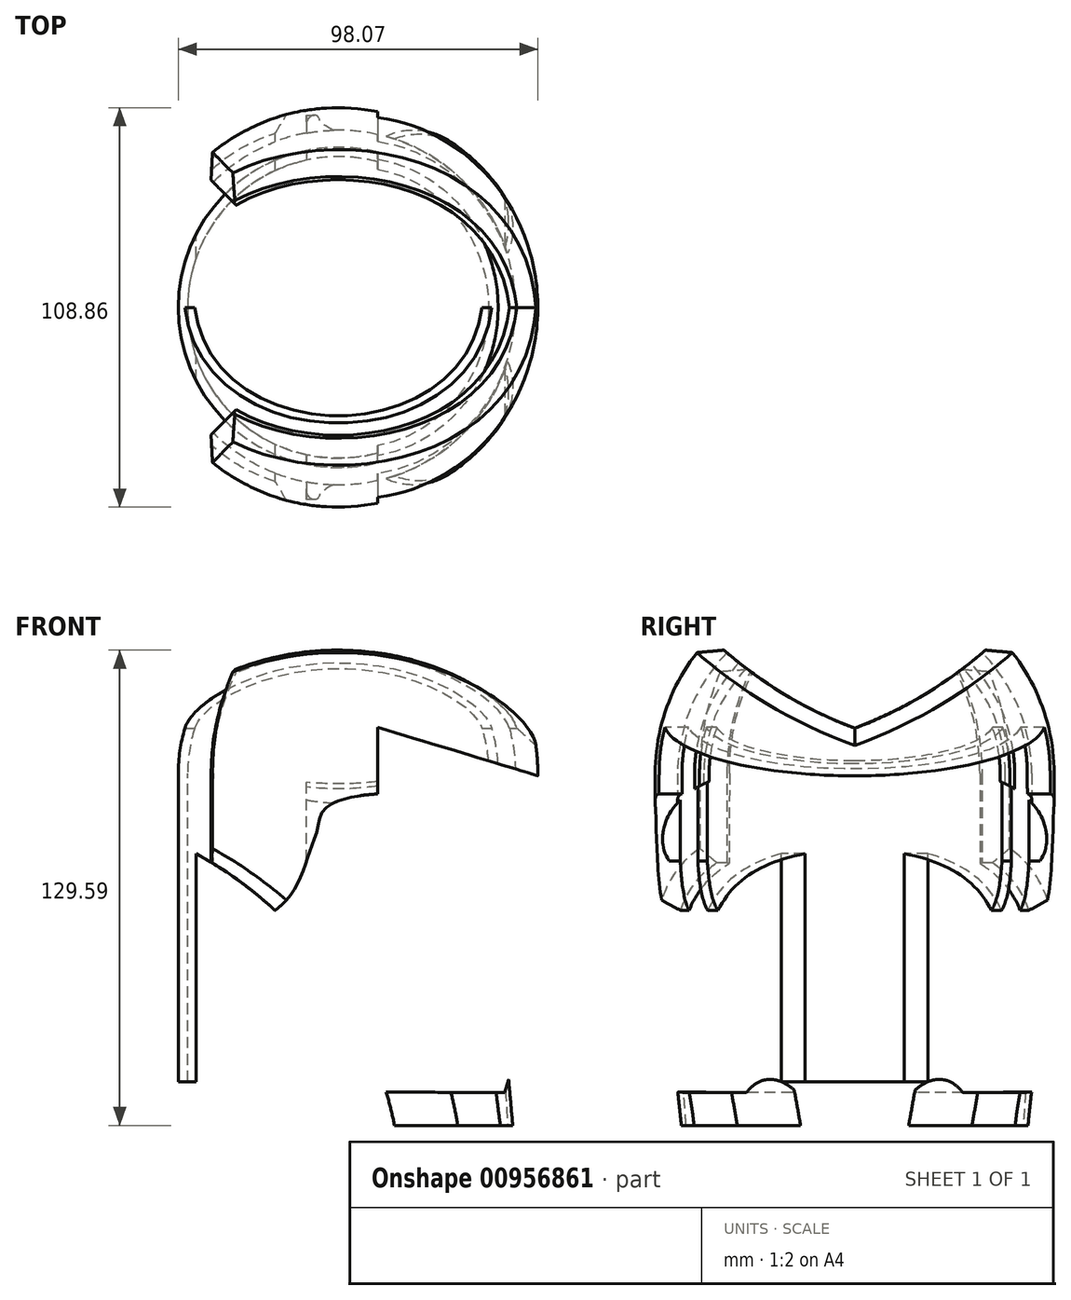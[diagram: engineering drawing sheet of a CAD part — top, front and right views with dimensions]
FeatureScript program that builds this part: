
annotation { "Feature Type Name" : "Feature", "Feature Type Description" : "" }
export const myFeature = defineFeature(function(context is Context, id is Id, definition is map)
    precondition{}
    {
        {
            var Q0;
            Q0=qCreatedBy(makeId("Front.planeOp"),FACE);
            var sketch = newSketch(context, id + "F0", { "sketchPlane" : qUnion([Q0])});
            skLineSegment(sketch, "E0", {"start": v(-40.6, -55.84) * mm, "end": v(-40.6, 28.21) * mm});
            skArc(sketch, "E1", {"start": v(3.06, 71.87) * mm, "mid": v(-27.8, 59.08) * mm, "end": v(-40.6, 28.21) * mm});
            skLineSegment(sketch, "E2", {"start": v(46.72, 28.21) * mm, "end": v(46.72, -55.84) * mm, "construction": true});
            skLineSegment(sketch, "E3", {"start": v(-40.6, -55.84) * mm, "end": v(46.72, -55.84) * mm, "construction": true});
            skLineSegment(sketch, "E4", {"start": v(3.06, 71.87) * mm, "end": v(3.06, -55.84) * mm});
            skArc(sketch, "E5.MirrorCS", {"start": v(3.06, 71.87) * mm, "mid": v(33.93, 59.08) * mm, "end": v(46.72, 28.21) * mm, "construction": true});
            skLineSegment(sketch, "E6", {"start": v(-40.6, -55.84) * mm, "end": v(3.06, -55.84) * mm});
            skLineSegment(sketch, "E7", {"start": v(7.59, 81.6) * mm, "end": v(7.59, 75.09) * mm});
            skArc(sketch, "E8", {"start": v(51.37, 28.17) * mm, "mid": v(38.7, 60.24) * mm, "end": v(7.59, 75.09) * mm});
            skLineSegment(sketch, "E9", {"start": v(51.37, 28.17) * mm, "end": v(51.53, -67.75) * mm});
            skLineSegment(sketch, "E10", {"start": v(51.53, -67.75) * mm, "end": v(57.63, -67.74) * mm});
            skLineSegment(sketch, "E11", {"start": v(57.63, -67.74) * mm, "end": v(57.48, 28.17) * mm});
            skArc(sketch, "E12", {"start": v(57.48, 28.17) * mm, "mid": v(43.04, 64.7) * mm, "end": v(7.59, 81.6) * mm});
            skSolve(sketch);
        }
        {
            var Q0;
            Q0=makeQuery(id+"F0.imprint","IMPRINT",FACE,{"disambiguationData":[TD([[makeQuery(id+"F0.imprint","IMPRINT",EDGE,{"derivedFrom":sQuery(id+"F0.wireOp",EDGE,"E0")}),-1.0]])]});
            var Q1;
            Q1=sQuery(id+"F0.wireOp",EDGE,"E4");
            revolve(context, id + "F1", {"surfaceOperationType" : NewSurfaceOperationType.NEW, "entities" : qUnion([Q0]), "axis" : qUnion([Q1]), "revolveType" : RevolveType.FULL});
        }
        {
            var Q0;
            Q0=makeQuery(id+"F0.imprint","IMPRINT",FACE,{"disambiguationData":[TD([[makeQuery(id+"F0.imprint","IMPRINT",EDGE,{"derivedFrom":sQuery(id+"F0.wireOp",EDGE,"E7")}),1.0]])]});
            var Q1;
            Q1=sQuery(id+"F0.wireOp",EDGE,"E4");
            revolve(context, id + "F2", {"surfaceOperationType" : NewSurfaceOperationType.NEW, "entities" : qUnion([Q0]), "axis" : qUnion([Q1]), "revolveType" : RevolveType.SYMMETRIC, "angle" : 270 * degree});
        }
        {
            var Q0;
            Q0=qCreatedBy(makeId("Right.planeOp"),FACE);
            cPlane(context, id + "F3", {"entities" : qUnion([Q0]), "cplaneType" : CPlaneType.OFFSET, "offset" : 85.1 * mm, "width" : 152.4 * mm, "height" : 152.4 * mm});
        }
        {
            var Q0;
            Q0=qCreatedBy(id+"F3.planeOp",FACE);
            var sketch = newSketch(context, id + "F4", { "sketchPlane" : qUnion([Q0])});
            skLineSegment(sketch, "E13", {"start": v(-13.97, -68.07) * mm, "end": v(-25.16, 1.69) * mm});
            skFitSpline(sketch, "E14", {"points": [v(-25.16, 1.69) * mm, v(-32.45, -1.14) * mm, v(-49.45, 3.04) * mm, v(-51.2, 15.86) * mm, v(-37.44, 26.79) * mm, v(-16.8, 26.25) * mm, v(-3.04, 20.58) * mm, v(0, 18.82) * mm], "startDerivative": vector(-53, -32.27) * mm, "endDerivative": vector(33.14, -20.3) * mm});
            skLineSegment(sketch, "E15", {"start": v(-13.97, -68.07) * mm, "end": v(0, -68.07) * mm});
            skFitSpline(sketch, "E16.MirrorCS", {"points": [v(25.16, 1.69) * mm, v(32.45, -1.14) * mm, v(49.45, 3.04) * mm, v(51.2, 15.86) * mm, v(37.44, 26.79) * mm, v(16.8, 26.25) * mm, v(3.04, 20.58) * mm, v(0, 18.82) * mm], "startDerivative": vector(53, -32.27) * mm, "endDerivative": vector(-33.14, -20.3) * mm});
            skLineSegment(sketch, "E17.MirrorCS", {"start": v(13.97, -68.07) * mm, "end": v(25.16, 1.69) * mm});
            skLineSegment(sketch, "E18.MirrorCS", {"start": v(13.97, -68.07) * mm, "end": v(0, -68.07) * mm});
            skSolve(sketch);
        }
        {
            var Q0;
            Q0=makeQuery(id+"F1.opRevolve","SWEPT_FACE",FACE,{"disambiguationData":[OSD([sQuery(id+"F0.wireOp",EDGE,"E6")])]});
            shell(context, id + "F5", {"entities" : qUnion([Q0]), "thickness" : 2.54 * mm});
        }
        {
            var Q0;
            Q0=makeQuery(id+"F4.imprint","IMPRINT",FACE,{"disambiguationData":[TD([[makeQuery(id+"F4.imprint","IMPRINT",EDGE,{"derivedFrom":sQuery(id+"F4.wireOp",EDGE,"E13")}),-1.0]])]});
            extrude(context, id + "F6", {"entities" : qUnion([Q0]), "operationType" : NewBodyOperationType.REMOVE, "oppositeDirection" : true, "depth" : 90.68 * mm, "offsetDistance" : 25.4 * mm});
        }
        {
            var Q0;
            Q0=qCreatedBy(id+"F3.planeOp",FACE);
            var sketch = newSketch(context, id + "F7", { "sketchPlane" : qUnion([Q0])});
            skArc(sketch, "E19", {"start": v(-43.65, 69.56) * mm, "mid": v(-23.5, 52.54) * mm, "end": v(0, 40.55) * mm});
            skArc(sketch, "E20", {"start": v(0, 84.13) * mm, "mid": v(-23.25, 81.1) * mm, "end": v(-43.65, 69.56) * mm});
            skArc(sketch, "E21.MirrorCS", {"start": v(0, 84.13) * mm, "mid": v(23.25, 81.1) * mm, "end": v(43.65, 69.56) * mm});
            skArc(sketch, "E22.MirrorCS", {"start": v(43.65, 69.56) * mm, "mid": v(23.5, 52.54) * mm, "end": v(0, 40.55) * mm});
            skSolve(sketch);
        }
        {
            var Q0;
            Q0=makeQuery(id+"F7.imprint","IMPRINT",FACE,{"disambiguationData":[TD([[makeQuery(id+"F7.imprint","IMPRINT",EDGE,{"derivedFrom":sQuery(id+"F7.wireOp",EDGE,"E19")}),1.0]])]});
            extrude(context, id + "F8", {"entities" : qUnion([Q0]), "operationType" : NewBodyOperationType.REMOVE, "oppositeDirection" : true, "depth" : 135.89 * mm, "offsetDistance" : 25.4 * mm});
        }
        {
            var Q0;
            Q0=qCreatedBy(makeId("Front.planeOp"),FACE);
            cPlane(context, id + "F9", {"entities" : qUnion([Q0]), "cplaneType" : CPlaneType.OFFSET, "offset" : 110.24 * mm, "width" : 152.4 * mm, "height" : 152.4 * mm});
        }
        {
            var Q0;
            Q0=qCreatedBy(id+"F9.planeOp",FACE);
            var sketch = newSketch(context, id + "F10", { "sketchPlane" : qUnion([Q0])});
            skFitSpline(sketch, "E23", {"points": [v(-9.82, -55.7) * mm, v(-8.65, -48.67) * mm, v(-10.78, -43.46) * mm, v(-13.34, -37.2) * mm, v(-16.86, -29.65) * mm, v(-19.2, -23) * mm, v(-21.03, -18.57) * mm, v(-19.6, -13.23) * mm, v(-15.3, -9.84) * mm, v(-11.26, -6.45) * mm, v(-7.22, 0) * mm, v(-4.35, 8.01) * mm, v(-2.66, 12.7) * mm, v(-1.61, 17.14) * mm, v(2.56, 20.52) * mm, v(13.63, 22.6) * mm, v(23.14, 22.22) * mm, v(29.14, 21.04) * mm, v(36.3, 18.96) * mm, v(44, 17.66) * mm, v(47.38, 18.96) * mm, v(47.64, 11.66) * mm, v(46.6, -2.28) * mm, v(46.73, -10.62) * mm, v(47.12, -15.18) * mm, v(47, -19.74) * mm, v(48.3, -27.7) * mm, v(48.95, -35.9) * mm, v(49.2, -43.59) * mm, v(50.25, -48.15) * mm, v(49.47, -55.32) * mm, v(47.12, -56.1) * mm], "startDerivative": vector(61.29, 216.68) * mm, "endDerivative": vector(-134.05, -1.03) * mm});
            skLineSegment(sketch, "E24", {"start": v(-9.82, -55.7) * mm, "end": v(47.12, -56.1) * mm});
            skLineSegment(sketch, "E25", {"start": v(-9.82, -55.7) * mm, "end": v(-9.82, -58.44) * mm});
            skLineSegment(sketch, "E26", {"start": v(-9.82, -58.44) * mm, "end": v(48.42, -58.84) * mm});
            skLineSegment(sketch, "E27", {"start": v(48.42, -58.84) * mm, "end": v(49.47, -55.32) * mm});
            skSolve(sketch);
        }
        {
            var Q0;
            Q0=makeQuery(id+"F10.imprint","IMPRINT",FACE,{"disambiguationData":[TD([[makeQuery(id+"F10.imprint","IMPRINT",EDGE,{"derivedFrom":sQuery(id+"F10.wireOp",EDGE,"E23")}),-1.0]])]});
            extrude(context, id + "F11", {"entities" : qUnion([Q0]), "operationType" : NewBodyOperationType.REMOVE, "oppositeDirection" : true, "depth" : 205.74 * mm, "offsetDistance" : 25.4 * mm});
        }
        {
            var Q0;
            {var subQ0=sQuery(id+"F10.wireOp",EDGE,"E24");Q0=makeQuery(id+"F10.imprint","IMPRINT",FACE,{"disambiguationData":[TD([[makeQuery(id+"F10.imprint","IMPRINT",EDGE,{"derivedFrom":subQ0}),-1.0]])]});}
            extrude(context, id + "F12", {"entities" : qUnion([Q0]), "operationType" : NewBodyOperationType.REMOVE, "oppositeDirection" : true, "depth" : 187.7 * mm, "offsetDistance" : 25.4 * mm});
        }
        {
            var Q0;
            Q0=qCreatedBy(id+"F9.planeOp",FACE);
            var sketch = newSketch(context, id + "F13", { "sketchPlane" : qUnion([Q0])});
            skArc(sketch, "E28", {"start": v(17.8, -69) * mm, "mid": v(-0.22, -25.11) * mm, "end": v(-35.76, 6.32) * mm});
            skLineSegment(sketch, "E29", {"start": v(-35.76, 6.32) * mm, "end": v(-35.76, -68.22) * mm});
            skLineSegment(sketch, "E30", {"start": v(-35.76, -68.22) * mm, "end": v(17.8, -69) * mm});
            skSolve(sketch);
        }
        {
            var Q0;
            Q0=makeQuery(id+"F13.imprint","IMPRINT",FACE,{"disambiguationData":[TD([[makeQuery(id+"F13.imprint","IMPRINT",EDGE,{"derivedFrom":sQuery(id+"F13.wireOp",EDGE,"E28")}),1.0]])]});
            extrude(context, id + "F14", {"entities" : qUnion([Q0]), "operationType" : NewBodyOperationType.REMOVE, "oppositeDirection" : true, "depth" : 192.02 * mm, "offsetDistance" : 25.4 * mm});
        }
        {
            var Q0;
            Q0=makeQuery(id+"F8.boolean.opBoolean","INTERSECT",EDGE,{"derivedFrom":[makeQuery(id+"F2.opRevolve","SWEPT_FACE",FACE,{"disambiguationData":[OSD([sQuery(id+"F0.wireOp",EDGE,"E12")])]}),makeQuery(id+"F8.opExtrude","SWEPT_FACE",FACE,{"disambiguationData":[OSD([sQuery(id+"F7.wireOp",EDGE,"E19")])]})]});
            var Q1;
            Q1=makeQuery(id+"F8.boolean.opBoolean","INTERSECT",EDGE,{"derivedFrom":[makeQuery(id+"F2.opRevolve","SWEPT_FACE",FACE,{"disambiguationData":[OSD([sQuery(id+"F0.wireOp",EDGE,"E12")])]}),makeQuery(id+"F8.opExtrude","SWEPT_FACE",FACE,{"disambiguationData":[OSD([sQuery(id+"F7.wireOp",EDGE,"E22.MirrorCS")])]})]});
            var Q2;
            Q2=makeQuery(id+"F14.boolean.opBoolean","INTERSECT",EDGE,{"disambiguationData":[OD(1.0)],"derivedFrom":[makeQuery(id+"F2.opRevolve","SWEPT_FACE",FACE,{"disambiguationData":[OSD([sQuery(id+"F0.wireOp",EDGE,"E11")])]}),makeQuery(id+"F14.opExtrude","SWEPT_FACE",FACE,{"disambiguationData":[OSD([sQuery(id+"F13.wireOp",EDGE,"E28")])]})]});
            var Q3;
            Q3=makeQuery(id+"F14.boolean.opBoolean","INTERSECT",EDGE,{"disambiguationData":[OD(0.0)],"derivedFrom":[makeQuery(id+"F2.opRevolve","SWEPT_FACE",FACE,{"disambiguationData":[OSD([sQuery(id+"F0.wireOp",EDGE,"E11")])]}),makeQuery(id+"F14.opExtrude","SWEPT_FACE",FACE,{"disambiguationData":[OSD([sQuery(id+"F13.wireOp",EDGE,"E28")])]})]});
            var Q4;
            Q4=makeQuery(id+"F6.boolean.opBoolean","INTERSECT",EDGE,{"derivedFrom":[makeQuery(id+"F2.opRevolve","SWEPT_FACE",FACE,{"disambiguationData":[OSD([sQuery(id+"F0.wireOp",EDGE,"E11")])]}),makeQuery(id+"F6.opExtrude","SWEPT_FACE",FACE,{"disambiguationData":[OSD([sQuery(id+"F4.wireOp",EDGE,"E17.MirrorCS")])]})]});
            var Q5;
            Q5=makeQuery(id+"F6.boolean.opBoolean","INTERSECT",EDGE,{"derivedFrom":[makeQuery(id+"F2.opRevolve","SWEPT_FACE",FACE,{"disambiguationData":[OSD([sQuery(id+"F0.wireOp",EDGE,"E11")])]}),makeQuery(id+"F6.opExtrude","SWEPT_FACE",FACE,{"disambiguationData":[OSD([sQuery(id+"F4.wireOp",EDGE,"E13")])]})]});
            chamfer(context, id + "F15", {"entities" : qUnion([Q0, Q1, Q2, Q3, Q4, Q5]), "width" : 5.08 * mm, "tangentPropagation" : true});
        }
        {
            var Q0;
            Q0=qCreatedBy(id+"F9.planeOp",FACE);
            var sketch = newSketch(context, id + "F16", { "sketchPlane" : qUnion([Q0])});
            skLineSegment(sketch, "E31.left", {"start": v(13.8, 40.76) * mm, "end": v(13.8, 15.96) * mm});
            skPoint(sketch, "E32.start.orphan", {"position": v(40.52, 23.3) * mm});
            skLineSegment(sketch, "E33", {"start": v(13.8, 40.76) * mm, "end": v(64.93, 25.32) * mm});
            skLineSegment(sketch, "E34", {"start": v(64.93, 15.96) * mm, "end": v(64.93, 13.56) * mm});
            skLineSegment(sketch, "E35", {"start": v(64.93, 13.56) * mm, "end": v(13.68, 13.56) * mm});
            skLineSegment(sketch, "E36", {"start": v(13.68, 13.56) * mm, "end": v(13.8, 15.96) * mm});
            skLineSegment(sketch, "E37", {"start": v(64.93, 15.96) * mm, "end": v(64.93, 25.32) * mm});
            skSolve(sketch);
        }
        {
            var Q0;
            Q0 = qSketchRegion(id + "F16", true);
            extrude(context, id + "F17", {"entities" : qUnion([Q0]), "operationType" : NewBodyOperationType.REMOVE, "oppositeDirection" : true, "depth" : 277.62 * mm, "offsetDistance" : 25.4 * mm});
        }
        {
            var Q0;
            Q0=makeQuery(id+"F2.opRevolve","CAP_EDGE",EDGE,{"disambiguationData":[OSD([sQuery(id+"F0.wireOp",EDGE,"E12")])],"isStart":true});
            var Q1;
            Q1=makeQuery(id+"F2.opRevolve","CAP_EDGE",EDGE,{"disambiguationData":[OSD([sQuery(id+"F0.wireOp",EDGE,"E12")])],"isStart":false});
            chamfer(context, id + "F18", {"entities" : qUnion([Q0, Q1]), "width" : 5.08 * mm, "tangentPropagation" : true});
        }
        {
            var Q0;
            {var subQ0=makeQuery(id+"F2.opRevolve","SWEPT_FACE",FACE,{"disambiguationData":[OSD([sQuery(id+"F0.wireOp",EDGE,"E12")])]});Q0=makeQuery(id+"F15.opChamfer","BLEND_EDGE",EDGE,{"blendedFrom":[makeQuery(id+"F8.boolean.opBoolean","INTERSECT",EDGE,{"derivedFrom":[subQ0,makeQuery(id+"F8.opExtrude","SWEPT_FACE",FACE,{"disambiguationData":[OSD([sQuery(id+"F7.wireOp",EDGE,"E19")])]})]}),subQ0],"blendedInto":[subQ0]});}
            var Q1;
            {var subQ0=makeQuery(id+"F2.opRevolve","SWEPT_FACE",FACE,{"disambiguationData":[OSD([sQuery(id+"F0.wireOp",EDGE,"E12")])]});Q1=makeQuery(id+"F15.opChamfer","BLEND_EDGE",EDGE,{"blendedFrom":[makeQuery(id+"F8.boolean.opBoolean","INTERSECT",EDGE,{"derivedFrom":[subQ0,makeQuery(id+"F8.opExtrude","SWEPT_FACE",FACE,{"disambiguationData":[OSD([sQuery(id+"F7.wireOp",EDGE,"E22.MirrorCS")])]})]}),subQ0],"blendedInto":[subQ0]});}
            var Q2;
            {var subQ0=makeQuery(id+"F2.opRevolve","SWEPT_FACE",FACE,{"disambiguationData":[OSD([sQuery(id+"F0.wireOp",EDGE,"E11")])]});Q2=makeQuery(id+"F15.opChamfer","BLEND_EDGE",EDGE,{"blendedFrom":[makeQuery(id+"F6.boolean.opBoolean","INTERSECT",EDGE,{"derivedFrom":[subQ0,makeQuery(id+"F6.opExtrude","SWEPT_FACE",FACE,{"disambiguationData":[OSD([sQuery(id+"F4.wireOp",EDGE,"E17.MirrorCS")])]})]}),subQ0],"blendedInto":[subQ0]});}
            var Q3;
            {var subQ0=makeQuery(id+"F2.opRevolve","SWEPT_FACE",FACE,{"disambiguationData":[OSD([sQuery(id+"F0.wireOp",EDGE,"E11")])]});Q3=makeQuery(id+"F15.opChamfer","BLEND_EDGE",EDGE,{"blendedFrom":[makeQuery(id+"F6.boolean.opBoolean","INTERSECT",EDGE,{"derivedFrom":[subQ0,makeQuery(id+"F6.opExtrude","SWEPT_FACE",FACE,{"disambiguationData":[OSD([sQuery(id+"F4.wireOp",EDGE,"E13")])]})]}),subQ0],"blendedInto":[subQ0]});}
            var Q4;
            {var subQ0=makeQuery(id+"F2.opRevolve","SWEPT_FACE",FACE,{"disambiguationData":[OSD([sQuery(id+"F0.wireOp",EDGE,"E11")])]});Q4=makeQuery(id+"F15.opChamfer","BLEND_EDGE",EDGE,{"blendedFrom":[makeQuery(id+"F14.boolean.opBoolean","INTERSECT",EDGE,{"disambiguationData":[OD(1.0)],"derivedFrom":[subQ0,makeQuery(id+"F14.opExtrude","SWEPT_FACE",FACE,{"disambiguationData":[OSD([sQuery(id+"F13.wireOp",EDGE,"E28")])]})]}),subQ0],"blendedInto":[subQ0]});}
            var Q5;
            {var subQ0=makeQuery(id+"F2.opRevolve","SWEPT_FACE",FACE,{"disambiguationData":[OSD([sQuery(id+"F0.wireOp",EDGE,"E11")])]});Q5=makeQuery(id+"F15.opChamfer","BLEND_EDGE",EDGE,{"blendedFrom":[makeQuery(id+"F14.boolean.opBoolean","INTERSECT",EDGE,{"disambiguationData":[OD(0.0)],"derivedFrom":[subQ0,makeQuery(id+"F14.opExtrude","SWEPT_FACE",FACE,{"disambiguationData":[OSD([sQuery(id+"F13.wireOp",EDGE,"E28")])]})]}),subQ0],"blendedInto":[subQ0]});}
            fillet(context, id + "F19", {"entities" : qUnion([Q0, Q1, Q2, Q3, Q4, Q5]), "radius" : 17.45 * mm, "tangentPropagation" : true, "allowEdgeOverflow" : false});
        }
    });
